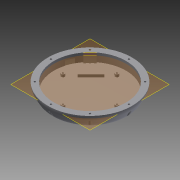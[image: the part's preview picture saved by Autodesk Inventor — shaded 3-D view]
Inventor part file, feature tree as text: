
AUTODESK INVENTOR PART (.ipt)
format: ipt  version: 2014 (Build 180170000, 170)  size: 332,288 bytes
history: native  units: mm
features: sketch x10, extrude x8, projected_geometry x7, plane x2, fillet x2, loft x1
ambient origin geometry x8: Origin, YZ Plane, XZ Plane, XY Plane, X Axis, Y Axis, Z Axis, Center Point
bodies: Solid1 (feature_tree)
feature tree (30):
  sketch  "Sketch1"  dims[d0=120.0mm d1=20.0mm d2=140.0mm]
  plane  "Work Plane1"
  loft  "Loft1"
  fillet  "Fillet1"  Radius=140.0mm
  extrude  "Extrusion1"  TaperAngle=0.0deg  [1 undecoded]
  extrude  "Extrusion2"  Depth=120.0mm
  extrude  "Extrusion3"  Depth=10.0mm
  fillet  "Fillet2"  Radius=5.5mm
  extrude  "Extrusion4"  Depth=5.5mm
  extrude  "Extrusion5"  TaperAngle=45.0deg  [1 undecoded]
  extrude  "Extrusion6"  Depth=5.5mm
  plane  "Work Plane2"
  extrude  "Extrusion7"  Depth=5.5mm
  extrude  "Extrusion8"  Depth=10.0mm TaperAngle=0.0deg
  sketch  "Sketch2"  dims[d3=0.0mm d4=90.0deg d5=0.0mm d6=90.0deg]
  sketch  "Sketch3"  dims[d7=20.0mm d8=120.0mm]
  sketch  "Sketch4"  dims[d9=10.0mm d10=0.0mm d11=130.0mm d12=5.5mm]
  sketch  "Sketch5"  dims[d13=5.5mm d14=5.5mm]
  sketch  "Sketch6"  dims[d15=5.5mm d16=45.0deg]
  projected_geometry  "Projected Loop1"
  projected_geometry  "Projected Loop2"
  projected_geometry  "Projected Loop3"
  projected_geometry  "Projected Loop4"
  projected_geometry  "Projected Loop5"
  projected_geometry  "Projected Loop6"
  projected_geometry  "Projected Loop7"
  sketch  "Sketch7"  dims[d17=5.5mm d18=5.5mm]
  sketch  "Sketch9"  dims[d19=5.5mm d20=5.5mm]
  sketch  "Sketch10"  dims[d21=10.0mm d22=0.0mm d23=4.0mm d24=0.0mm]
  sketch  "Sketch11"  dims[d25=20.0mm d26=3.0mm d27=3.0mm d28=3.0mm d29=3.0mm d30=3.0mm d31=3.0mm d32=3.0mm d33=3.0mm d34=4.0mm d35=0.0mm d36=90.0mm d37=6.0mm d38=2.5mm d39=6.0mm d40=2.5mm d41=6.0mm d42=2.5mm d43=6.0mm d44=2.5mm d45=4.0mm d46=0.0mm d47=4.0mm d48=0.0mm d49=36.75mm d50=16.0mm d51=17.5mm d52=29.0mm d53=0.0mm d54=0.6mm d55=12.0mm d56=10.0mm d57=35.0mm d58=0.0mm]
note: 2 required parameter values undecoded (feature->parameter linkage not recoverable at this tier; creation-order binding heuristic only, values carry confidence <= 0.55)
